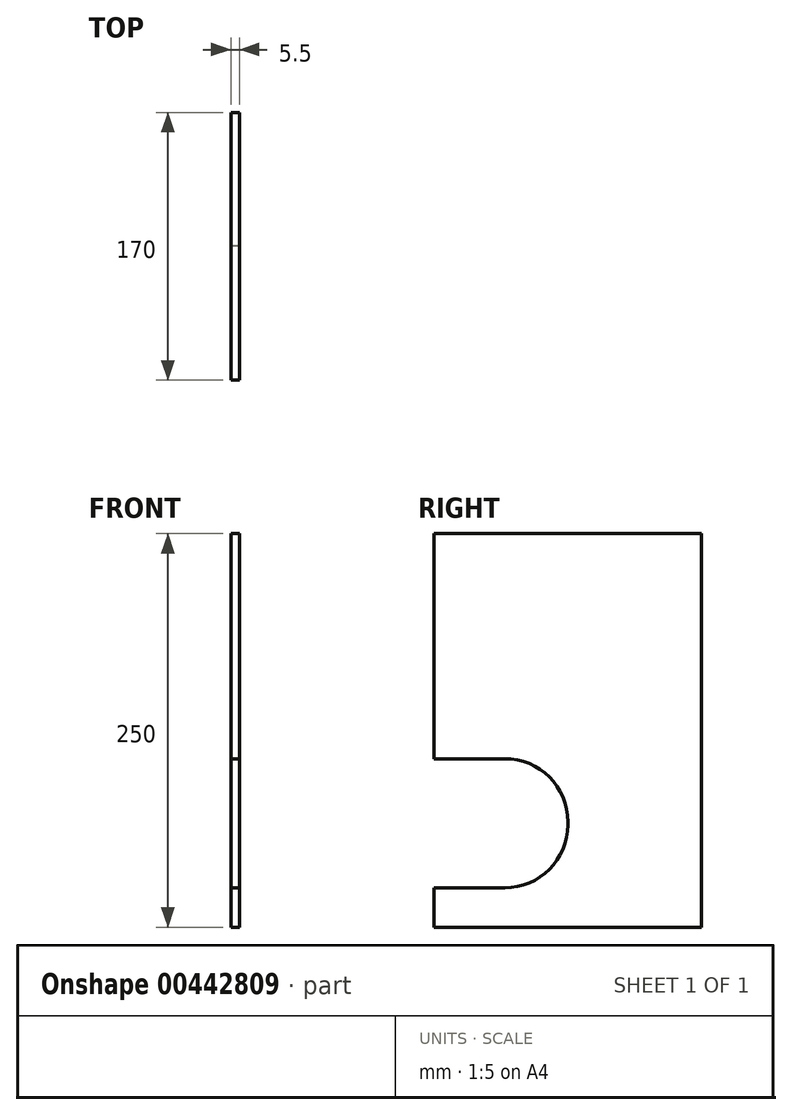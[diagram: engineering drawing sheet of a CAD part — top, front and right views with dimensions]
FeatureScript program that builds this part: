
annotation { "Feature Type Name" : "Feature", "Feature Type Description" : "" }
export const myFeature = defineFeature(function(context is Context, id is Id, definition is map)
    precondition{}
    {
        {
            var Q0;
            Q0=qCreatedBy(makeId("Right.planeOp"),FACE);
            var sketch = newSketch(context, id + "F0", { "sketchPlane" : qUnion([Q0])});
            skLineSegment(sketch, "E0.bottom", {"start": v(0, 0) * mm, "end": v(-170, 0) * mm});
            skLineSegment(sketch, "E0.top", {"start": v(-60, 250) * mm, "end": v(-170, 250) * mm});
            skLineSegment(sketch, "E0.left", {"start": v(0, 0) * mm, "end": v(0, 190) * mm});
            skLineSegment(sketch, "E0.right", {"start": v(-170, 0) * mm, "end": v(-170, 25) * mm});
            skLineSegment(sketch, "E1.bottom", {"start": v(-170, 25) * mm, "end": v(-125, 25) * mm});
            skLineSegment(sketch, "E1.top", {"start": v(-170, 107) * mm, "end": v(-125, 107) * mm});
            skLineSegment(sketch, "E1.right", {"start": v(-85, 65) * mm, "end": v(-85, 67) * mm});
            skPoint(sketch, "E2.visualSharp", {"position": v(-85, 107) * mm});
            skArc(sketch, "E2.filletArc", {"start": v(-85, 67) * mm, "mid": v(-96.72, 95.28) * mm, "end": v(-125, 107) * mm});
            skLineSegment(sketch, "E3.trimOffspring", {"start": v(-170, 107) * mm, "end": v(-170, 250) * mm});
            skPoint(sketch, "E4.visualSharp", {"position": v(0, 250) * mm});
            skPoint(sketch, "E5.visualSharp", {"position": v(-85, 25) * mm});
            skArc(sketch, "E5.filletArc", {"start": v(-125, 25) * mm, "mid": v(-96.72, 36.72) * mm, "end": v(-85, 65) * mm});
            skLineSegment(sketch, "E6", {"start": v(-60, 250) * mm, "end": v(0, 250) * mm});
            skLineSegment(sketch, "E7", {"start": v(0, 250) * mm, "end": v(0, 190) * mm});
            skSolve(sketch);
        }
        {
            var Q0;
            Q0 = qSketchRegion(id + "F0", true);
            extrude(context, id + "F1", {"entities" : qUnion([Q0]), "depth" : 5.5 * mm, "offsetDistance" : 25 * mm});
        }
    });
